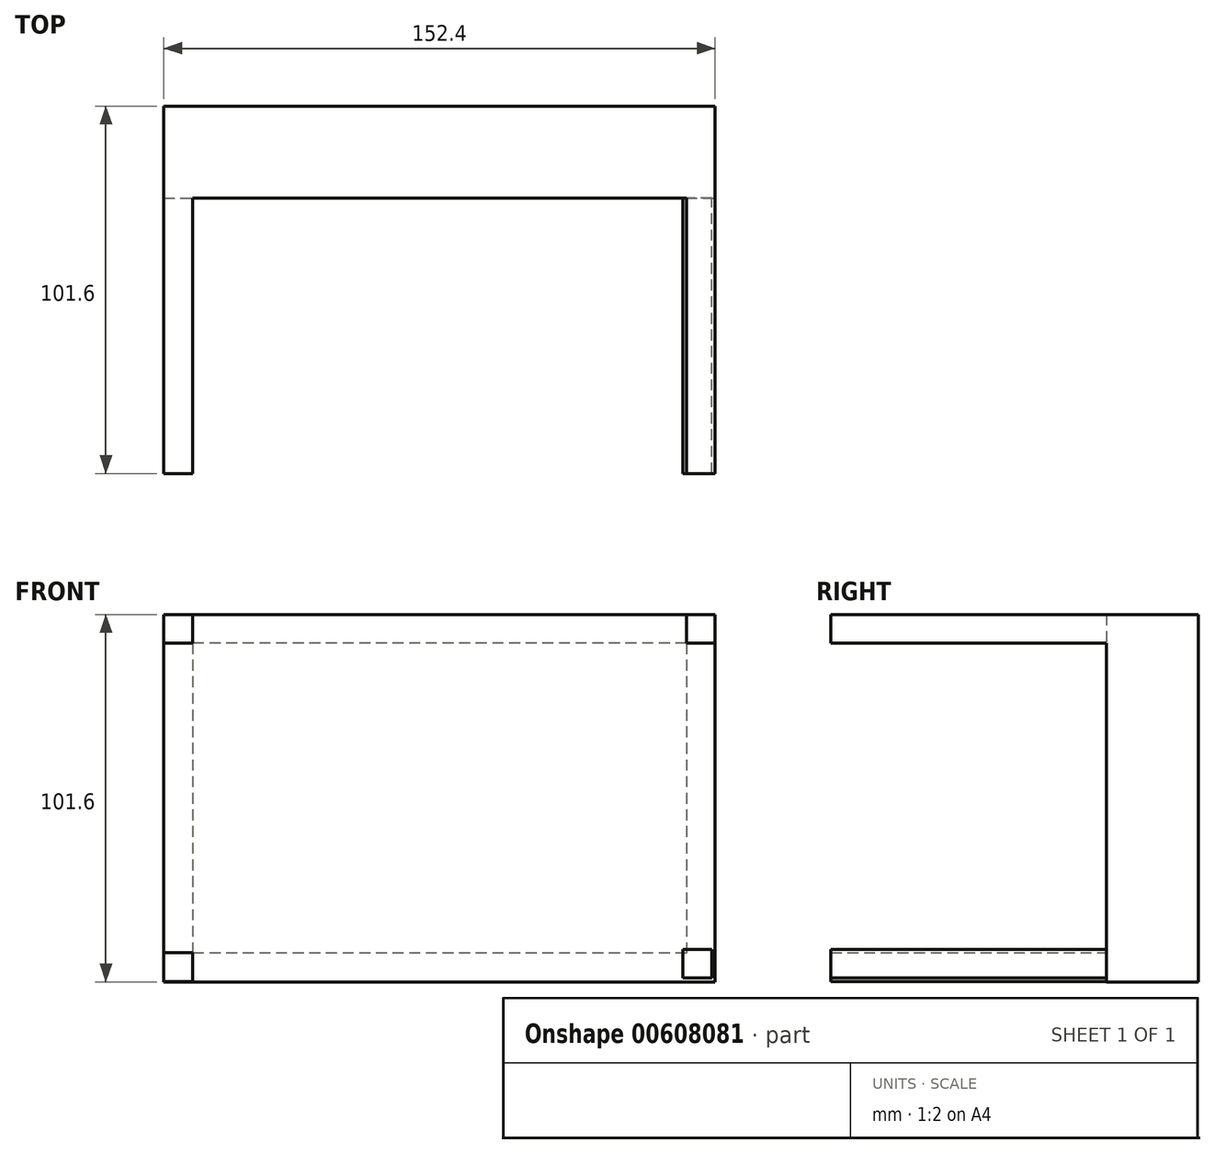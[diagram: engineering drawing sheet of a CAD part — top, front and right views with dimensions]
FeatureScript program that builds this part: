
annotation { "Feature Type Name" : "Feature", "Feature Type Description" : "" }
export const myFeature = defineFeature(function(context is Context, id is Id, definition is map)
    precondition{}
    {
        {
            var Q0;
            Q0=qCreatedBy(makeId("Front.planeOp"),FACE);
            var sketch = newSketch(context, id + "F0", { "sketchPlane" : qUnion([Q0])});
            skLineSegment(sketch, "E0.bottom", {"start": v(-158.58, 90.38) * mm, "end": v(-6.18, 90.38) * mm});
            skLineSegment(sketch, "E0.top", {"start": v(-158.58, -11.22) * mm, "end": v(-6.18, -11.22) * mm});
            skLineSegment(sketch, "E0.left", {"start": v(-158.58, 90.38) * mm, "end": v(-158.58, -11.22) * mm});
            skLineSegment(sketch, "E0.right", {"start": v(-6.18, 90.38) * mm, "end": v(-6.18, -11.22) * mm});
            skSolve(sketch);
        }
        {
            var Q0;
            Q0=makeQuery(id+"F0.imprint","IMPRINT",FACE,{"disambiguationData":[TD([[makeQuery(id+"F0.imprint","IMPRINT",EDGE,{"derivedFrom":sQuery(id+"F0.wireOp",EDGE,"E0.bottom")}),-1.0]])]});
            extrude(context, id + "F1", {"entities" : qUnion([Q0]), "depth" : 25.4 * mm, "offsetDistance" : 25.4 * mm});
        }
        {
            var Q0;
            Q0=makeQuery(id+"F1.opExtrude","CAP_FACE",FACE,{"disambiguationData":[OSD([sQuery(id+"F0.wireOp",EDGE,"E0.bottom"),sQuery(id+"F0.wireOp",EDGE,"E0.top"),sQuery(id+"F0.wireOp",EDGE,"E0.left"),sQuery(id+"F0.wireOp",EDGE,"E0.right")])],"isStart":false});
            var sketch = newSketch(context, id + "F2", { "sketchPlane" : qUnion([Q0])});
            skLineSegment(sketch, "E1.bottom", {"start": v(-158.58, 82.44) * mm, "end": v(-150.65, 82.44) * mm});
            skLineSegment(sketch, "E1.top", {"start": v(-158.58, 90.38) * mm, "end": v(-150.65, 90.38) * mm});
            skLineSegment(sketch, "E1.left", {"start": v(-158.58, 82.44) * mm, "end": v(-158.58, 90.38) * mm});
            skLineSegment(sketch, "E1.right", {"start": v(-150.65, 82.44) * mm, "end": v(-150.65, 90.38) * mm});
            skSolve(sketch);
        }
        {
            var Q0;
            Q0=makeQuery(id+"F2.imprint","IMPRINT",FACE,{"disambiguationData":[TD([[makeQuery(id+"F2.imprint","IMPRINT",EDGE,{"derivedFrom":sQuery(id+"F2.wireOp",EDGE,"E1.bottom")}),1.0]])]});
            extrude(context, id + "F3", {"entities" : qUnion([Q0]), "operationType" : NewBodyOperationType.ADD, "depth" : 76.2 * mm, "offsetDistance" : 25.4 * mm});
        }
        {
            var Q0;
            Q0=makeQuery(id+"F1.opExtrude","CAP_FACE",FACE,{"disambiguationData":[OSD([sQuery(id+"F0.wireOp",EDGE,"E0.bottom"),sQuery(id+"F0.wireOp",EDGE,"E0.top"),sQuery(id+"F0.wireOp",EDGE,"E0.left"),sQuery(id+"F0.wireOp",EDGE,"E0.right")])],"isStart":false});
            var sketch = newSketch(context, id + "F4", { "sketchPlane" : qUnion([Q0])});
            skLineSegment(sketch, "E2.bottom", {"start": v(-14.12, 90.38) * mm, "end": v(-6.18, 90.38) * mm});
            skLineSegment(sketch, "E2.top", {"start": v(-14.12, 82.44) * mm, "end": v(-6.18, 82.44) * mm});
            skLineSegment(sketch, "E2.left", {"start": v(-14.12, 90.38) * mm, "end": v(-14.12, 82.44) * mm});
            skLineSegment(sketch, "E2.right", {"start": v(-6.18, 90.38) * mm, "end": v(-6.18, 82.44) * mm});
            skSolve(sketch);
        }
        {
            var Q0;
            {var subQ2=sQuery(id+"F4.wireOp",EDGE,"E2.top");Q0=makeQuery(id+"F4.imprint","IMPRINT",FACE,{"disambiguationData":[TD([[makeQuery(id+"F4.imprint","IMPRINT",EDGE,{"derivedFrom":subQ2}),-1.0]])]});}
            var sketch = newSketch(context, id + "F5", { "sketchPlane" : qUnion([Q0])});
            skLineSegment(sketch, "E3.bottom", {"start": v(-158.56, -3.18) * mm, "end": v(-150.62, -3.18) * mm});
            skLineSegment(sketch, "E3.top", {"start": v(-158.56, -11.12) * mm, "end": v(-150.62, -11.12) * mm});
            skLineSegment(sketch, "E3.left", {"start": v(-158.56, -3.18) * mm, "end": v(-158.56, -11.12) * mm});
            skLineSegment(sketch, "E3.right", {"start": v(-150.62, -3.18) * mm, "end": v(-150.62, -11.12) * mm});
            skSolve(sketch);
        }
        {
            var Q0;
            Q0=makeQuery(id+"F5.imprint","IMPRINT",FACE,{"disambiguationData":[TD([[makeQuery(id+"F5.imprint","IMPRINT",EDGE,{"derivedFrom":sQuery(id+"F5.wireOp",EDGE,"E3.bottom")}),1.0]])]});
            var sketch = newSketch(context, id + "F6", { "sketchPlane" : qUnion([Q0])});
            skLineSegment(sketch, "E4.bottom", {"start": v(-7.1, -10.16) * mm, "end": v(-15.04, -10.16) * mm});
            skLineSegment(sketch, "E4.top", {"start": v(-7.1, -2.22) * mm, "end": v(-15.04, -2.22) * mm});
            skLineSegment(sketch, "E4.left", {"start": v(-7.1, -10.16) * mm, "end": v(-7.1, -2.22) * mm});
            skLineSegment(sketch, "E4.right", {"start": v(-15.04, -10.16) * mm, "end": v(-15.04, -2.22) * mm});
            skSolve(sketch);
        }
        {
            var Q0;
            Q0=makeQuery(id+"F4.imprint","IMPRINT",FACE,{"disambiguationData":[TD([[makeQuery(id+"F4.imprint","IMPRINT",EDGE,{"derivedFrom":sQuery(id+"F4.wireOp",EDGE,"E2.bottom")}),-1.0]])]});
            extrude(context, id + "F7", {"entities" : qUnion([Q0]), "operationType" : NewBodyOperationType.ADD, "depth" : 76.2 * mm, "offsetDistance" : 25.4 * mm});
        }
        {
            var Q0;
            Q0=makeQuery(id+"F5.imprint","IMPRINT",FACE,{"disambiguationData":[TD([[makeQuery(id+"F5.imprint","IMPRINT",EDGE,{"derivedFrom":sQuery(id+"F5.wireOp",EDGE,"E3.bottom")}),-1.0]])]});
            extrude(context, id + "F8", {"entities" : qUnion([Q0]), "operationType" : NewBodyOperationType.ADD, "depth" : 76.2 * mm, "offsetDistance" : 25.4 * mm});
        }
        {
            var Q0;
            Q0=makeQuery(id+"F6.imprint","IMPRINT",FACE,{"disambiguationData":[TD([[makeQuery(id+"F6.imprint","IMPRINT",EDGE,{"derivedFrom":sQuery(id+"F6.wireOp",EDGE,"E4.bottom")}),-1.0]])]});
            extrude(context, id + "F9", {"entities" : qUnion([Q0]), "operationType" : NewBodyOperationType.ADD, "depth" : 76.2 * mm, "offsetDistance" : 25.4 * mm});
        }
        {
            var Q0;
            Q0=makeQuery(id+"F1.opExtrude","CAP_FACE",FACE,{"disambiguationData":[OSD([sQuery(id+"F0.wireOp",EDGE,"E0.bottom"),sQuery(id+"F0.wireOp",EDGE,"E0.top"),sQuery(id+"F0.wireOp",EDGE,"E0.left"),sQuery(id+"F0.wireOp",EDGE,"E0.right")])],"isStart":true});
            var sketch = newSketch(context, id + "F10", { "sketchPlane" : qUnion([Q0])});
            skLineSegment(sketch, "E5.bottom", {"start": v(14.12, 82.44) * mm, "end": v(150.65, 82.44) * mm});
            skLineSegment(sketch, "E5.top", {"start": v(14.12, -3.28) * mm, "end": v(150.65, -3.28) * mm});
            skLineSegment(sketch, "E5.left", {"start": v(14.12, 82.44) * mm, "end": v(14.12, -3.28) * mm});
            skLineSegment(sketch, "E5.right", {"start": v(150.65, 82.44) * mm, "end": v(150.65, -3.28) * mm});
            skSolve(sketch);
        }
        {
            var Q0;
            Q0=makeQuery(id+"F10.imprint","IMPRINT",FACE,{"disambiguationData":[TD([[makeQuery(id+"F10.imprint","IMPRINT",EDGE,{"derivedFrom":sQuery(id+"F10.wireOp",EDGE,"E5.bottom")}),-1.0]])]});
            extrude(context, id + "F11", {"entities" : qUnion([Q0]), "operationType" : NewBodyOperationType.REMOVE, "oppositeDirection" : true, "depth" : 1 / 50.8 * mm, "offsetDistance" : 25.4 * mm});
        }
    });
